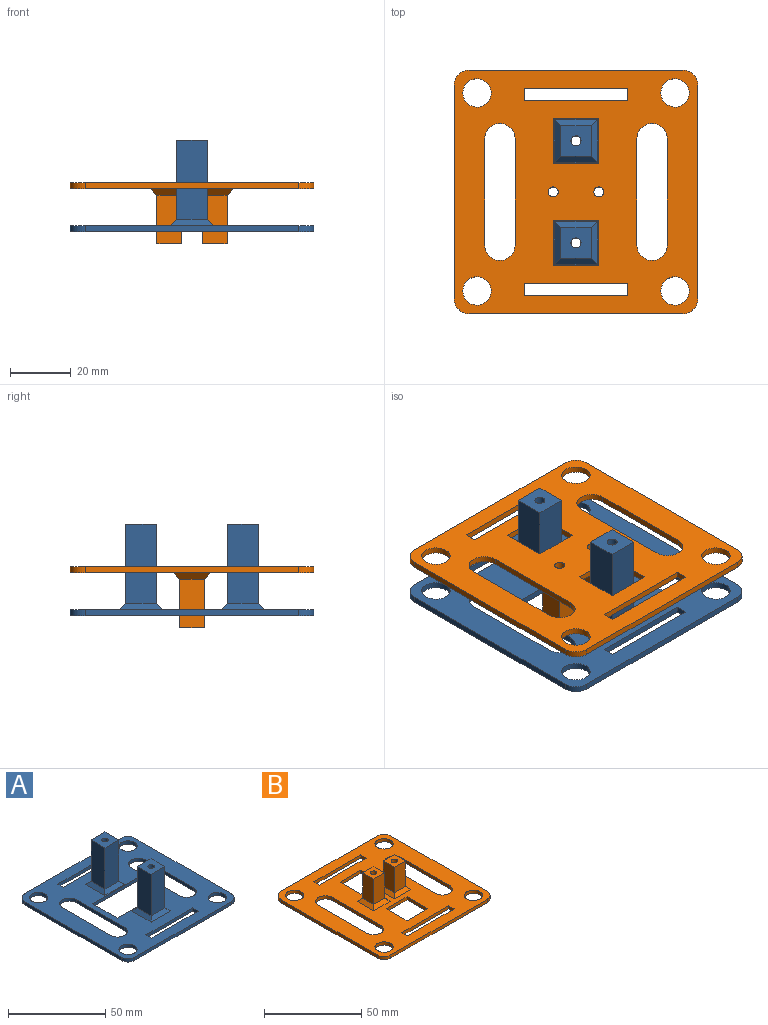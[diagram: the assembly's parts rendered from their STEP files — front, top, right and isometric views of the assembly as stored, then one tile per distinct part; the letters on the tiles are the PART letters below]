
ASSEMBLY  parts=2 mates=1
PART A: 54 faces, bbox 80x80x30 mm
  f0: plane 80x80mm, normal (0,0,-1), area 4357.3mm2, adj f5,f11,f14,f15,f16,f17,f18,f19
  f1: plane 80x80mm, normal (0,0,1), area 3982.4mm2, adj f14,f15,f16,f17,f18,f19,f20,f21
  f2: plane 26x10mm, normal (0,1,0), area 260mm2, adj f3,f6,f7,f35
  f3: plane 26x10mm, normal (-1,0,0), area 260mm2, adj f2,f4,f7,f37
  f4: plane 26x10mm, normal (0,-1,0), area 260mm2, adj f3,f6,f7,f36
  f5: cylinder r=1.65mm len=30mm, axis (0,0,-1), area 311mm2, adj f0,f7
  f6: plane 26x10mm, normal (1,0,0), area 260mm2, adj f2,f4,f7,f34
  f7: plane 10x10mm, normal (0,0,1), area 91.4mm2, adj f2,f3,f4,f5,f6
  f8: plane 26x10mm, normal (0,1,0), area 260mm2, adj f9,f12,f13,f31
  f9: plane 26x10mm, normal (-1,0,0), area 260mm2, adj f8,f10,f13,f33
  f10: plane 26x10mm, normal (0,-1,0), area 260mm2, adj f9,f12,f13,f32
  f11: cylinder r=1.65mm len=30mm, axis (0,0,-1), area 311mm2, adj f0,f13
  f12: plane 26x10mm, normal (1,0,0), area 260mm2, adj f8,f10,f13,f30
  f13: plane 10x10mm, normal (0,0,1), area 91.4mm2, adj f8,f9,f10,f11,f12
  f14: plane 33.5x2mm, normal (0,-1,0), area 67mm2, adj f0,f1,f15,f25
  f15: plane 18.01x2mm, normal (-1,0,0), area 36mm2, adj f0,f1,f14,f16
  f16: plane 33.5x2mm, normal (0,1,0), area 67mm2, adj f0,f1,f15,f25
  f17: plane 70x2mm, normal (-1,0,0), area 140mm2, adj f0,f1,f26,f29
  f18: plane 70x2mm, normal (0,-1,0), area 140mm2, adj f0,f1,f26,f27
  f19: plane 70x2mm, normal (1,0,0), area 140mm2, adj f0,f1,f27,f28
  f20: cylinder r=4.65mm len=9.3mm, axis (0,0,-1), area 58.4mm2, adj f0,f1
  f21: cylinder r=4.65mm len=9.3mm, axis (0,0,-1), area 58.4mm2, adj f0,f1
  f22: cylinder r=4.65mm len=9.3mm, axis (0,0,-1), area 58.4mm2, adj f0,f1
  f23: cylinder r=4.65mm len=9.3mm, axis (0,0,-1), area 58.4mm2, adj f0,f1
  f24: plane 70x2mm, normal (0,1,0), area 140mm2, adj f0,f1,f28,f29
  f25: plane 18.01x2mm, normal (1,0,0), area 36mm2, adj f0,f1,f14,f16
  f26: cylinder r=5mm len=5mm, axis (0,0,1), area 15.7mm2, adj f0,f1,f17,f18
  f27: cylinder r=5mm len=5mm, axis (0,0,-1), area 15.7mm2, adj f0,f1,f18,f19
  f28: cylinder r=5mm len=5mm, axis (0,0,1), area 15.7mm2, adj f0,f1,f19,f24
  f29: cylinder r=5mm len=5mm, axis (0,0,-1), area 15.7mm2, adj f0,f1,f17,f24
  f30: plane 14x2mm, normal (0.71,0,0.71), area 33.9mm2, adj f1,f12,f31,f32
  f31: plane 14x2mm, normal (0,0.71,0.71), area 33.9mm2, adj f1,f8,f30,f33
  f32: plane 14x2mm, normal (0,-0.71,0.71), area 33.9mm2, adj f1,f10,f30,f33
  f33: plane 14x2mm, normal (-0.71,0,0.71), area 33.9mm2, adj f1,f9,f31,f32
  f34: plane 14x2mm, normal (0.71,0,0.71), area 33.9mm2, adj f1,f6,f35,f36
  f35: plane 14x2mm, normal (0,0.71,0.71), area 33.9mm2, adj f1,f2,f34,f37
  f36: plane 14x2mm, normal (0,-0.71,0.71), area 33.9mm2, adj f1,f4,f34,f37
  f37: plane 14x2mm, normal (-0.71,0,0.71), area 33.9mm2, adj f1,f3,f35,f36
  f38: plane 34x2mm, normal (0,-1,0), area 68mm2, adj f0,f1,f39,f41
  f39: plane 4x2mm, normal (1,0,0), area 8mm2, adj f0,f1,f38,f40
  f40: plane 34x2mm, normal (0,1,0), area 68mm2, adj f0,f1,f39,f41
  f41: plane 4x2mm, normal (-1,0,0), area 8mm2, adj f0,f1,f38,f40
  f42: cylinder r=5mm len=10mm, axis (0,0,1), area 31.4mm2, adj f0,f1,f43,f45
  f43: plane 35x2mm, normal (1,0,0), area 70mm2, adj f0,f1,f42,f44
  f44: cylinder r=5mm len=10mm, axis (0,0,1), area 31.4mm2, adj f0,f1,f43,f45
  f45: plane 35x2mm, normal (-1,0,0), area 70mm2, adj f0,f1,f42,f44
  f46: plane 34x2mm, normal (0,-1,0), area 68mm2, adj f0,f1,f47,f49
  f47: plane 4x2mm, normal (1,0,0), area 8mm2, adj f0,f1,f46,f48
  f48: plane 34x2mm, normal (0,1,0), area 68mm2, adj f0,f1,f47,f49
  f49: plane 4x2mm, normal (-1,0,0), area 8mm2, adj f0,f1,f46,f48
  f50: cylinder r=5mm len=10mm, axis (0,0,1), area 31.4mm2, adj f0,f1,f51,f53
  f51: plane 35x2mm, normal (1,0,0), area 70mm2, adj f0,f1,f50,f52
  f52: cylinder r=5mm len=10mm, axis (0,0,1), area 31.4mm2, adj f0,f1,f51,f53
  f53: plane 35x2mm, normal (-1,0,0), area 70mm2, adj f0,f1,f50,f52
PART B: 58 faces, bbox 80x80x20 mm
  f0: plane 80x80mm, normal (0,0,-1), area 4510.6mm2, adj f5,f11,f14,f15,f16,f17,f18,f19
  f1: plane 80x80mm, normal (0,0,1), area 4239.7mm2, adj f14,f15,f16,f17,f18,f19,f20,f21
  f2: plane 16x8mm, normal (0,1,0), area 128mm2, adj f3,f6,f7,f35
  f3: plane 16x8mm, normal (-1,0,0), area 128mm2, adj f2,f4,f7,f39
  f4: plane 16x8mm, normal (0,-1,0), area 128mm2, adj f3,f6,f7,f37
  f5: cylinder r=1.65mm len=20mm, axis (0,0,-1), area 207.3mm2, adj f0,f7
  f6: plane 16x8mm, normal (1,0,0), area 128mm2, adj f2,f4,f7,f38
  f7: plane 8x8mm, normal (0,0,1), area 55.4mm2, adj f2,f3,f4,f5,f6
  f8: plane 16x8mm, normal (0,1,0), area 128mm2, adj f9,f12,f13,f34
  f9: plane 16x8mm, normal (-1,0,0), area 128mm2, adj f8,f10,f13,f40
  f10: plane 16x8mm, normal (0,-1,0), area 128mm2, adj f9,f12,f13,f36
  f11: cylinder r=1.65mm len=20mm, axis (0,0,-1), area 207.3mm2, adj f0,f13
  f12: plane 16x8mm, normal (1,0,0), area 128mm2, adj f8,f10,f13,f41
  f13: plane 8x8mm, normal (0,0,1), area 55.4mm2, adj f8,f9,f10,f11,f12
  f14: plane 15x2mm, normal (1,0,0), area 30mm2, adj f0,f1,f15,f26
  f15: plane 15x2mm, normal (0,-1,0), area 30mm2, adj f0,f1,f14,f16
  f16: plane 15x2mm, normal (-1,0,0), area 30mm2, adj f0,f1,f15,f26
  f17: plane 15x2mm, normal (1,0,0), area 30mm2, adj f0,f1,f18,f27
  f18: plane 15x2mm, normal (0,-1,0), area 30mm2, adj f0,f1,f17,f19
  f19: plane 15x2mm, normal (-1,0,0), area 30mm2, adj f0,f1,f18,f27
  f20: plane 70x2mm, normal (-1,0,0), area 140mm2, adj f0,f1,f30,f33
  f21: plane 70x2mm, normal (0,-1,0), area 140mm2, adj f0,f1,f30,f31
  f22: plane 70x2mm, normal (1,0,0), area 140mm2, adj f0,f1,f31,f32
  f23: cylinder r=4.65mm len=9.3mm, axis (0,0,-1), area 58.4mm2, adj f0,f1
  f24: cylinder r=4.65mm len=9.3mm, axis (0,0,-1), area 58.4mm2, adj f0,f1
  f25: cylinder r=4.65mm len=9.3mm, axis (0,0,-1), area 58.4mm2, adj f0,f1
  f26: plane 15x2mm, normal (0,1,0), area 30mm2, adj f0,f1,f14,f16
  f27: plane 15x2mm, normal (0,1,0), area 30mm2, adj f0,f1,f17,f19
  f28: plane 70x2mm, normal (0,1,0), area 140mm2, adj f0,f1,f32,f33
  f29: cylinder r=4.65mm len=9.3mm, axis (0,0,-1), area 58.4mm2, adj f0,f1
  f30: cylinder r=5mm len=5mm, axis (0,0,1), area 15.7mm2, adj f0,f1,f20,f21
  f31: cylinder r=5mm len=5mm, axis (0,0,-1), area 15.7mm2, adj f0,f1,f21,f22
  f32: cylinder r=5mm len=5mm, axis (0,0,1), area 15.7mm2, adj f0,f1,f22,f28
  f33: cylinder r=5mm len=5mm, axis (0,0,-1), area 15.7mm2, adj f0,f1,f20,f28
  f34: plane 12x2mm, normal (0,0.71,0.71), area 28.3mm2, adj f1,f8,f40,f41
  f35: plane 12x2mm, normal (0,0.71,0.71), area 28.3mm2, adj f1,f2,f38,f39
  f36: plane 12x2mm, normal (0,-0.71,0.71), area 28.3mm2, adj f1,f10,f40,f41
  f37: plane 12x2mm, normal (0,-0.71,0.71), area 28.3mm2, adj f1,f4,f38,f39
  f38: plane 12x2mm, normal (0.71,0,0.71), area 28.3mm2, adj f1,f6,f35,f37
  f39: plane 12x2mm, normal (-0.71,0,0.71), area 28.3mm2, adj f1,f3,f35,f37
  f40: plane 12x2mm, normal (-0.71,0,0.71), area 28.3mm2, adj f1,f9,f34,f36
  f41: plane 12x2mm, normal (0.71,0,0.71), area 28.3mm2, adj f1,f12,f34,f36
  f42: plane 34x2mm, normal (0,-1,0), area 68mm2, adj f0,f1,f43,f45
  f43: plane 4x2mm, normal (1,0,0), area 8mm2, adj f0,f1,f42,f44
  f44: plane 34x2mm, normal (0,1,0), area 68mm2, adj f0,f1,f43,f45
  f45: plane 4x2mm, normal (-1,0,0), area 8mm2, adj f0,f1,f42,f44
  f46: plane 34x2mm, normal (0,-1,0), area 68mm2, adj f0,f1,f47,f49
  f47: plane 4x2mm, normal (1,0,0), area 8mm2, adj f0,f1,f46,f48
  f48: plane 34x2mm, normal (0,1,0), area 68mm2, adj f0,f1,f47,f49
  f49: plane 4x2mm, normal (-1,0,0), area 8mm2, adj f0,f1,f46,f48
  f50: cylinder r=5mm len=10mm, axis (0,0,1), area 31.4mm2, adj f0,f1,f51,f53
  f51: plane 35x2mm, normal (1,0,0), area 70mm2, adj f0,f1,f50,f52
  f52: cylinder r=5mm len=10mm, axis (0,0,1), area 31.4mm2, adj f0,f1,f51,f53
  f53: plane 35x2mm, normal (-1,0,0), area 70mm2, adj f0,f1,f50,f52
  f54: cylinder r=5mm len=10mm, axis (0,0,1), area 31.4mm2, adj f0,f1,f55,f57
  f55: plane 35x2mm, normal (1,0,0), area 70mm2, adj f0,f1,f54,f56
  f56: cylinder r=5mm len=10mm, axis (0,0,1), area 31.4mm2, adj f0,f1,f55,f57
  f57: plane 35x2mm, normal (-1,0,0), area 70mm2, adj f0,f1,f54,f56
PLACE A t=(-7.27,-9.28,25.12)mm
PLACE B rot(axis=(1,0,0),180deg) t=(-47.69,31.7,41.12)mm
MATE slider B.f25 <-> A.f21  axis (0,0,-1) through (-40.19,-40.8,39.12)mm
